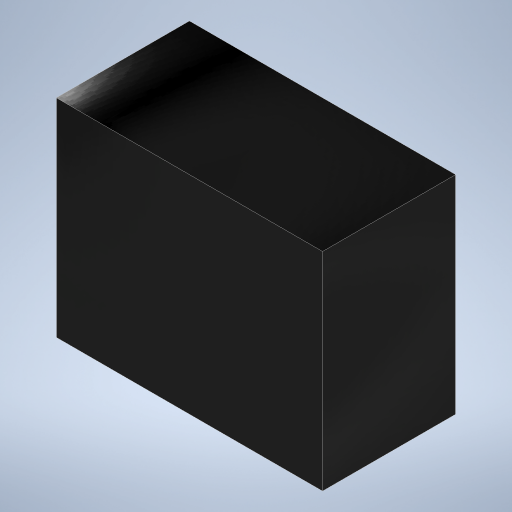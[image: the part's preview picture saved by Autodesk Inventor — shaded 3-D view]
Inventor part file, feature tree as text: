
AUTODESK INVENTOR PART (.ipt)
format: ipt  version: 2023 (Build 270158000, 158)  size: 179,200 bytes
history: native  units: mm
features: extrude x1, sketch x1
ambient origin geometry x8: Origin, YZ Plane, XZ Plane, XY Plane, X Axis, Y Axis, Z Axis, Center Point
bodies: Volumenkörper1 (feature_tree)
feature tree (2):
  extrude  "Extrusion1"  Depth=3.4mm
  sketch  "Skizze1"  dims[d0=2.65mm d1=3.4mm d2=1.7mm d3=0.0mm]
